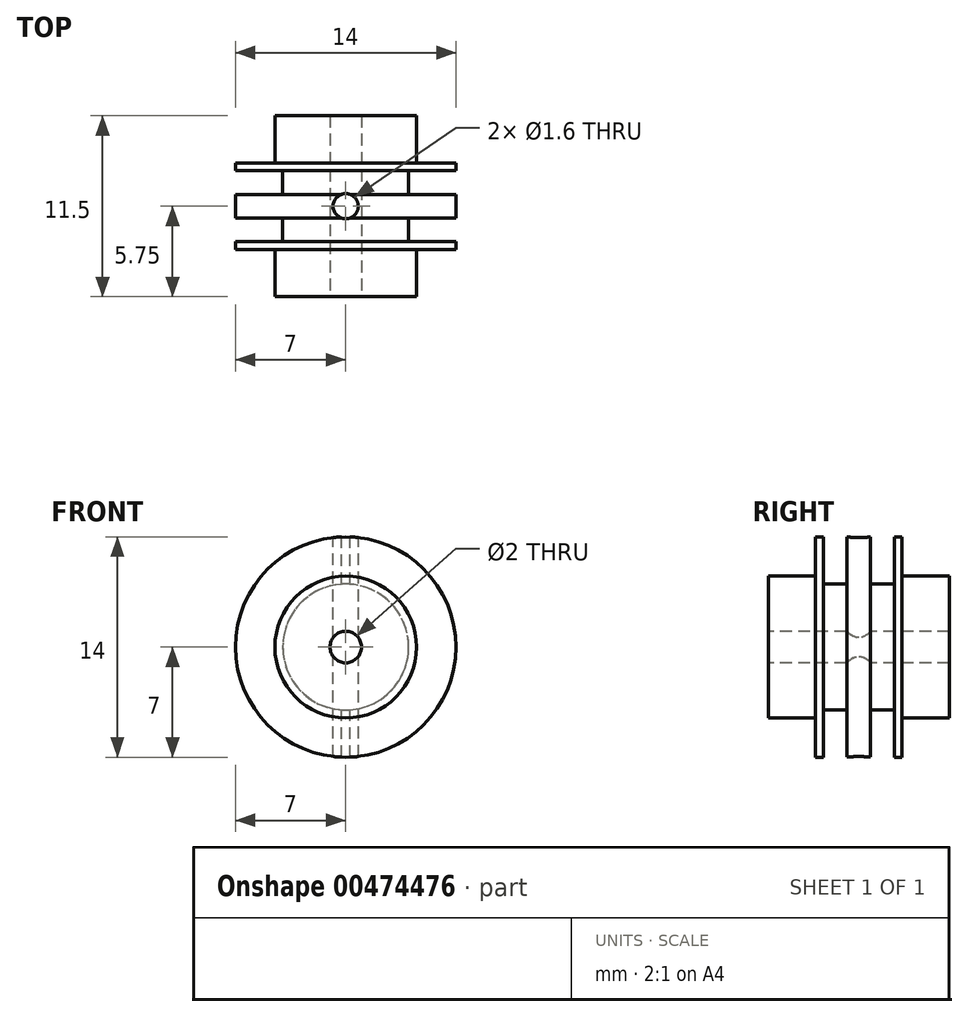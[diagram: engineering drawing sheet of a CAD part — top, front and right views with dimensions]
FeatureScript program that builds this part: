
annotation { "Feature Type Name" : "Feature", "Feature Type Description" : "" }
export const myFeature = defineFeature(function(context is Context, id is Id, definition is map)
    precondition{}
    {
        {
            var Q0;
            Q0=qCreatedBy(makeId("Right.planeOp"),FACE);
            var sketch = newSketch(context, id + "F0", { "sketchPlane" : qUnion([Q0])});
            skLineSegment(sketch, "E0.bottom", {"start": v(0, 0) * mm, "end": v(5.5, 0) * mm});
            skLineSegment(sketch, "E0.top", {"start": v(0, 7) * mm, "end": v(0.5, 7) * mm});
            skLineSegment(sketch, "E0.left", {"start": v(0, 0) * mm, "end": v(0, 7) * mm});
            skLineSegment(sketch, "E0.right", {"start": v(5.5, 0) * mm, "end": v(5.5, 7) * mm});
            skLineSegment(sketch, "E1", {"start": v(0.5, 7) * mm, "end": v(0.5, 4) * mm});
            skLineSegment(sketch, "E2", {"start": v(0.5, 4) * mm, "end": v(2, 4) * mm});
            skLineSegment(sketch, "E3", {"start": v(2, 4) * mm, "end": v(2, 7) * mm});
            skLineSegment(sketch, "E4", {"start": v(3.5, 7) * mm, "end": v(3.5, 4) * mm});
            skLineSegment(sketch, "E5", {"start": v(3.5, 4) * mm, "end": v(5, 4) * mm});
            skLineSegment(sketch, "E6", {"start": v(5, 4) * mm, "end": v(5, 7) * mm});
            skLineSegment(sketch, "E7.trimOffspring", {"start": v(2, 7) * mm, "end": v(3.5, 7) * mm});
            skLineSegment(sketch, "E8.trimOffspring", {"start": v(5, 7) * mm, "end": v(5.5, 7) * mm});
            skLineSegment(sketch, "E9", {"start": v(-5.1, 0) * mm, "end": v(10.5, 0) * mm, "construction": true});
            skLineSegment(sketch, "E10", {"start": v(0, 4.5) * mm, "end": v(-3, 4.5) * mm});
            skLineSegment(sketch, "E11", {"start": v(-3, 4.5) * mm, "end": v(-3, 0) * mm});
            skLineSegment(sketch, "E12", {"start": v(5.5, 4.5) * mm, "end": v(8.5, 4.5) * mm});
            skLineSegment(sketch, "E13", {"start": v(8.5, 4.5) * mm, "end": v(8.5, 0) * mm});
            skLineSegment(sketch, "E14", {"start": v(8.5, 0) * mm, "end": v(5.5, 0) * mm});
            skLineSegment(sketch, "E15", {"start": v(0, 0) * mm, "end": v(-3, 0) * mm});
            skSolve(sketch);
        }
        {
            var Q0;
            Q0=makeQuery(id+"F0.imprint","IMPRINT",FACE,{"disambiguationData":[TD([[makeQuery(id+"F0.imprint","IMPRINT",EDGE,{"derivedFrom":sQuery(id+"F0.wireOp",EDGE,"E0.bottom")}),1.0]])]});
            var Q1;
            {var subQ2=sQuery(id+"F0.wireOp",EDGE,"E12");Q1=makeQuery(id+"F0.imprint","IMPRINT",FACE,{"disambiguationData":[TD([[makeQuery(id+"F0.imprint","IMPRINT",EDGE,{"derivedFrom":subQ2}),-1.0]])]});}
            var Q2;
            {var subQ2=sQuery(id+"F0.wireOp",EDGE,"E10");Q2=makeQuery(id+"F0.imprint","IMPRINT",FACE,{"disambiguationData":[TD([[makeQuery(id+"F0.imprint","IMPRINT",EDGE,{"derivedFrom":subQ2}),1.0]])]});}
            var Q3;
            Q3=sQuery(id+"F0.wireOp",EDGE,"E9");
            revolve(context, id + "F1", {"entities" : qUnion([Q0, Q1, Q2]), "axis" : qUnion([Q3]), "revolveType" : RevolveType.FULL});
        }
        {
            var Q0;
            Q0=qCreatedBy(makeId("Top.planeOp"),FACE);
            var sketch = newSketch(context, id + "F2", { "sketchPlane" : qUnion([Q0])});
            skCircle(sketch, "E16", {"center": v(0, 2.75) * mm, "radius": 0.8 * mm});
            skSolve(sketch);
        }
        {
            var Q0;
            Q0 = qSketchRegion(id + "F2", true);
            extrude(context, id + "F3", {"entities" : qUnion([Q0]), "operationType" : NewBodyOperationType.REMOVE, "oppositeDirection" : true, "depth" : 25 * mm});
        }
        {
            var Q0;
            Q0 = qSketchRegion(id + "F2", true);
            extrude(context, id + "F4", {"entities" : qUnion([Q0]), "operationType" : NewBodyOperationType.REMOVE, "oppositeDirection" : true, "depth" : 25 * mm, "hasSecondDirection" : true, "secondDirectionOppositeDirection" : false, "secondDirectionDepth" : 25 * mm});
        }
        {
            var Q0;
            Q0=makeQuery(id+"F1.opRevolve","SWEPT_FACE",FACE,{"disambiguationData":[OSD([sQuery(id+"F0.wireOp",EDGE,"E11")])]});
            var sketch = newSketch(context, id + "F5", { "sketchPlane" : qUnion([Q0])});
            skCircle(sketch, "E17", {"center": v(0, 0) * mm, "radius": 1 * mm});
            skSolve(sketch);
        }
        {
            var Q0;
            Q0 = qSketchRegion(id + "F5", true);
            extrude(context, id + "F6", {"entities" : qUnion([Q0]), "operationType" : NewBodyOperationType.REMOVE, "oppositeDirection" : true, "depth" : 25 * mm});
        }
    });
